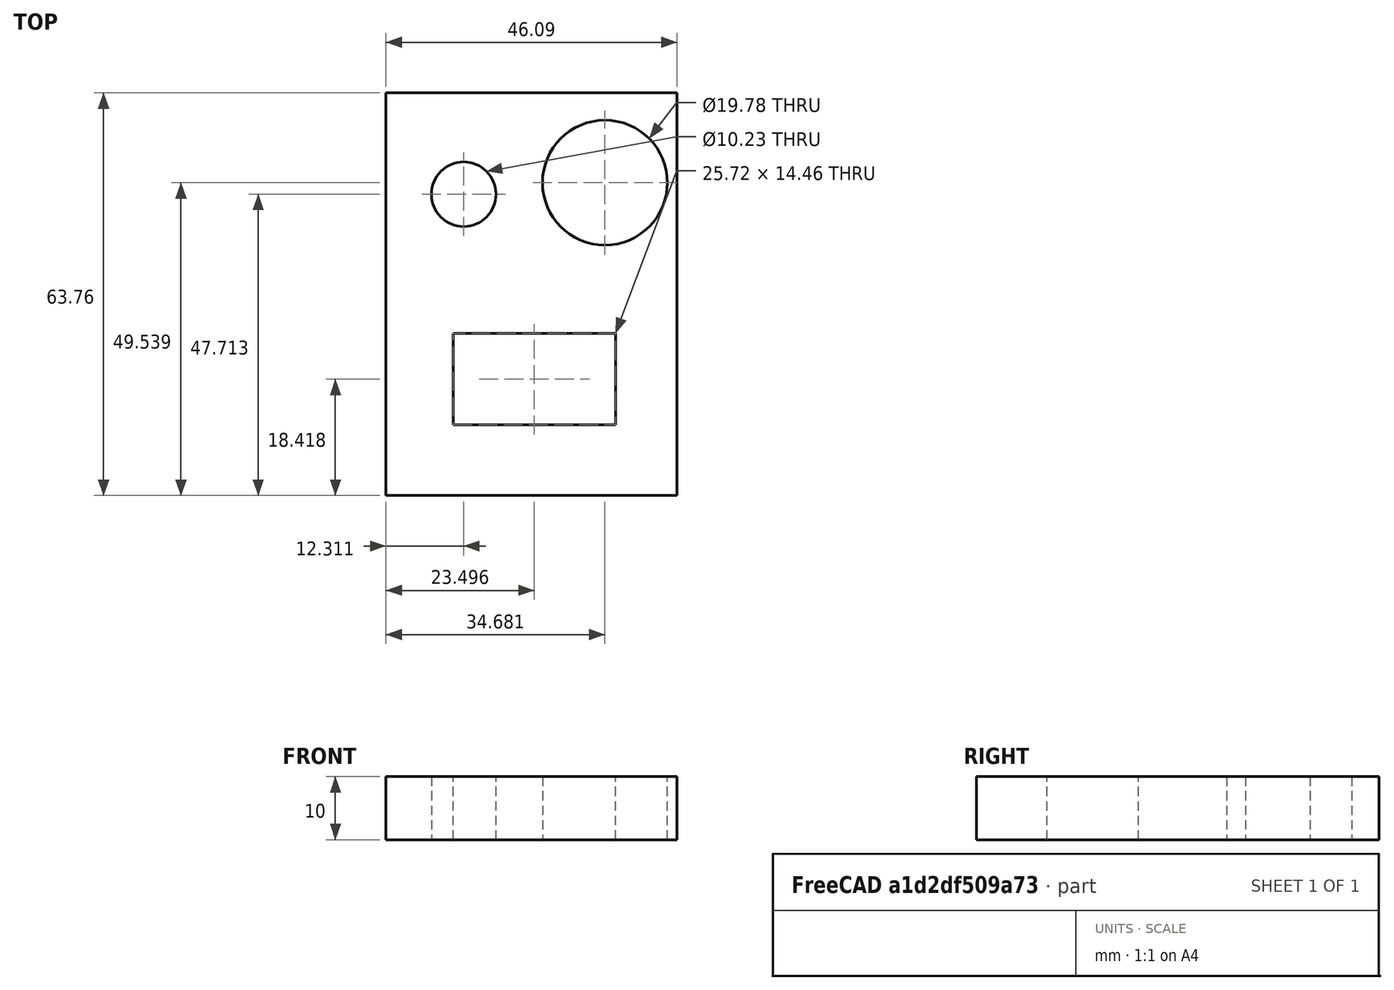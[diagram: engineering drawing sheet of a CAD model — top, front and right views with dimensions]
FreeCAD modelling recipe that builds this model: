
FCSTD DOCUMENT  (FreeCAD 1.0R38806 (Git))
Label: Cara-robot
License: All rights reserved
LicenseURL: https://en.wikipedia.org/wiki/All_rights_reserved
objects: Sketcher::SketchObject×1, Part::Extrusion×1
note: 3 computed .brp shape members not serialized (recipe doc carries the construction recipe); baked Part::Feature solids carry a one-line shape summary decoded from their .brp

FEATURE [Sketcher::SketchObject] Sketch
  ArcFitTolerance = 1e-06
  FullyConstrained = false
  MakeInternals = false
  sketch-geometry (10):
    g0: LineSegment StartX=-24.1636 StartY=30.8551 StartZ=0 EndX=-24.1636 EndY=-32.8995 EndZ=0
    g1: LineSegment StartX=-24.1636 StartY=-32.8995 StartZ=0 EndX=21.933 EndY=-32.8995 EndZ=0
    g2: LineSegment StartX=21.933 StartY=-32.8995 StartZ=0 EndX=21.933 EndY=30.8551 EndZ=0
    g3: LineSegment StartX=21.933 StartY=30.8551 StartZ=0 EndX=-24.1636 EndY=30.8551 EndZ=0
    g4: Circle CenterX=-11.8494 CenterY=14.8131 CenterZ=0 NormalX=0 NormalY=0 NormalZ=1 AngleXU=0 Radius=5.1156
    g5: Circle CenterX=10.5212 CenterY=16.6393 CenterZ=0 NormalX=0 NormalY=0 NormalZ=1 AngleXU=0 Radius=9.89173
    g6: LineSegment StartX=-13.5234 StartY=-7.25308 StartZ=0 EndX=-13.5234 EndY=-21.7102 EndZ=0
    g7: LineSegment StartX=-13.5234 StartY=-21.7102 StartZ=0 EndX=12.1951 EndY=-21.7102 EndZ=0
    g8: LineSegment StartX=12.1951 StartY=-21.7102 StartZ=0 EndX=12.1951 EndY=-7.25308 EndZ=0
    g9: LineSegment StartX=12.1951 StartY=-7.25308 StartZ=0 EndX=-13.5234 EndY=-7.25308 EndZ=0
  constraints (16):
    c: Coincident(g0,g1)
    c: Coincident(g1,g2)
    c: Coincident(g2,g3)
    c: Coincident(g3,g0)
    c: Vertical(g0)
    c: Vertical(g2)
    c: Horizontal(g1)
    c: Horizontal(g3)
    c: Coincident(g6,g7)
    c: Coincident(g7,g8)
    c: Coincident(g8,g9)
    c: Coincident(g9,g6)
    c: Vertical(g6)
    c: Vertical(g8)
    c: Horizontal(g7)
    c: Horizontal(g9)
FEATURE [Part::Extrusion] Extrude
  Base = -> Sketch
  Dir = (0,0,1)
  DirMode = 2
  FaceMakerClass = Part::FaceMakerBullseye
  FaceMakerMode = 3
  LengthFwd = 10
  LengthRev = 0
  Solid = true
  Symmetric = false
